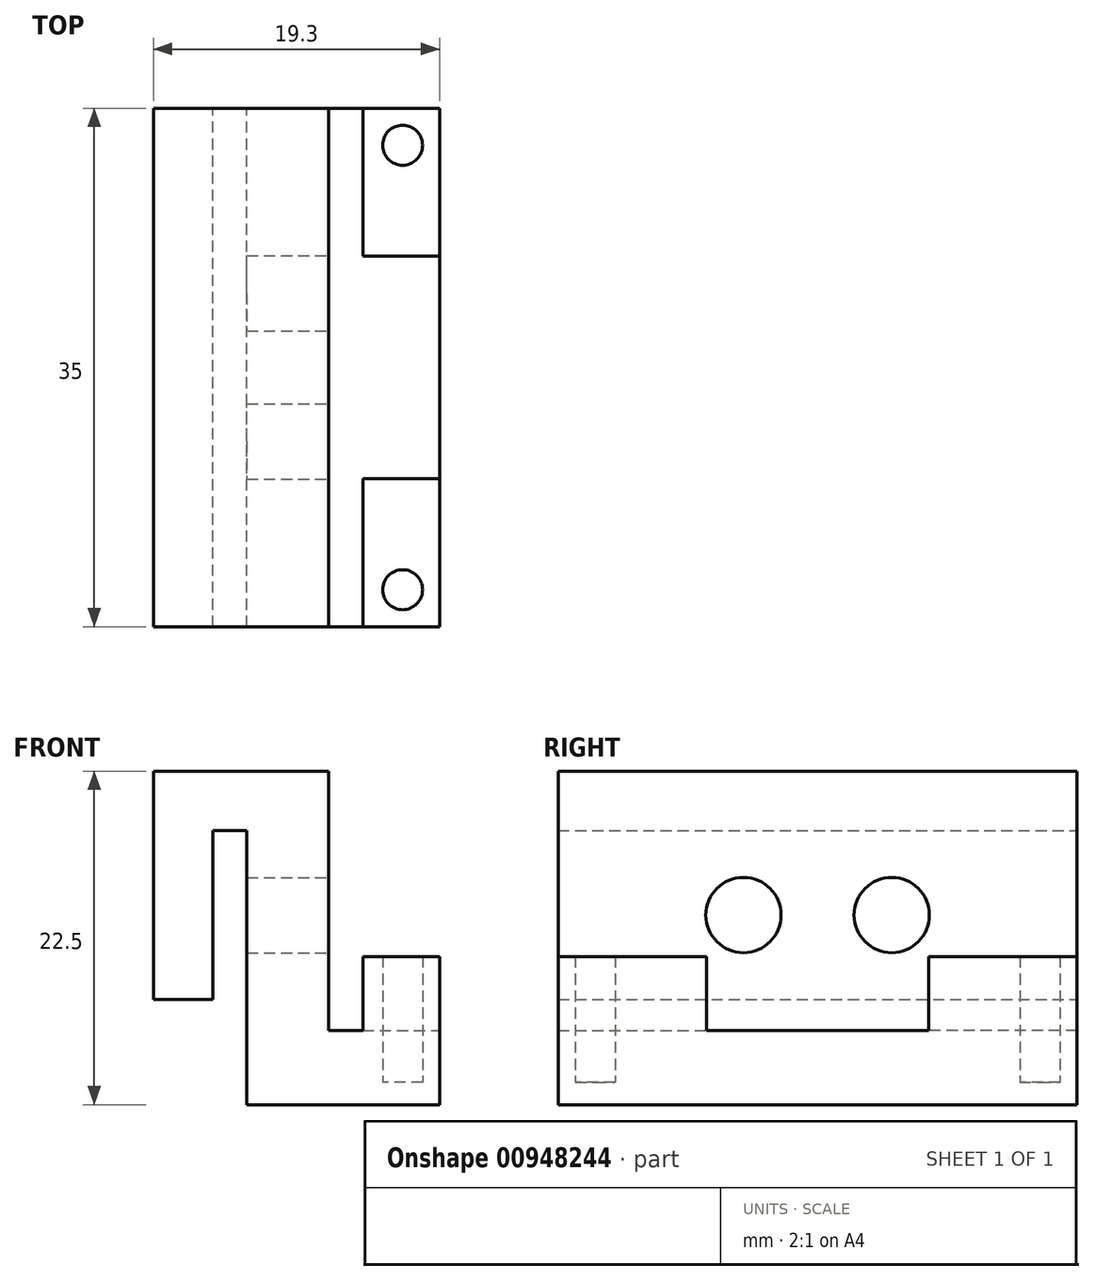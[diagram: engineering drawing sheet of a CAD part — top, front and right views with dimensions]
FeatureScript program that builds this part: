
annotation { "Feature Type Name" : "Feature", "Feature Type Description" : "" }
export const myFeature = defineFeature(function(context is Context, id is Id, definition is map)
    precondition{}
    {
        {
            var Q0;
            Q0=qCreatedBy(makeId("Front.planeOp"),FACE);
            var sketch = newSketch(context, id + "F0", { "sketchPlane" : qUnion([Q0])});
            skLineSegment(sketch, "E0", {"start": v(-36.46, 19.1) * mm, "end": v(-36.46, 34.5) * mm});
            skLineSegment(sketch, "E1", {"start": v(-36.46, 34.5) * mm, "end": v(-24.66, 34.5) * mm});
            skLineSegment(sketch, "E2", {"start": v(-24.66, 34.5) * mm, "end": v(-24.66, 17) * mm});
            skLineSegment(sketch, "E3", {"start": v(-17.16, 12) * mm, "end": v(-30.16, 12) * mm});
            skLineSegment(sketch, "E4", {"start": v(-30.16, 12) * mm, "end": v(-30.16, 30.5) * mm});
            skLineSegment(sketch, "E5", {"start": v(-30.16, 30.5) * mm, "end": v(-32.46, 30.5) * mm});
            skLineSegment(sketch, "E6", {"start": v(-32.46, 30.5) * mm, "end": v(-32.46, 19.1) * mm});
            skLineSegment(sketch, "E7", {"start": v(-32.46, 19.1) * mm, "end": v(-36.46, 19.1) * mm});
            skLineSegment(sketch, "E8", {"start": v(-24.66, 17) * mm, "end": v(-17.16, 17) * mm});
            skLineSegment(sketch, "E9", {"start": v(-17.16, 17) * mm, "end": v(-17.16, 12) * mm});
            skSolve(sketch);
        }
        {
            var Q0;
            Q0=qSketchRegion(id+"F0",true);
            extrude(context, id + "F1", {"entities" : qUnion([Q0]), "depth" : 35 * mm, "offsetDistance" : 25 * mm});
        }
        {
            var Q0;
            Q0=makeQuery(id+"F1.opExtrude","SWEPT_FACE",FACE,{"disambiguationData":[OSD([sQuery(id+"F0.wireOp",EDGE,"E8")])]});
            var sketch = newSketch(context, id + "F2", { "sketchPlane" : qUnion([Q0])});
            skLineSegment(sketch, "E10", {"start": v(-19.66, 0) * mm, "end": v(-19.66, -35) * mm, "construction": true});
            skLineSegment(sketch, "E11", {"start": v(-19.66, -2.5) * mm, "end": v(-17.16, -2.5) * mm, "construction": true});
            skLineSegment(sketch, "E12", {"start": v(-19.66, -32.5) * mm, "end": v(-17.16, -32.5) * mm, "construction": true});
            skLineSegment(sketch, "E13.bottom", {"start": v(-22.34, 0) * mm, "end": v(-17.16, 0) * mm});
            skLineSegment(sketch, "E13.top", {"start": v(-22.34, -10) * mm, "end": v(-17.16, -10) * mm});
            skLineSegment(sketch, "E13.left", {"start": v(-22.34, 0) * mm, "end": v(-22.34, -10) * mm});
            skLineSegment(sketch, "E13.right", {"start": v(-17.16, 0) * mm, "end": v(-17.16, -10) * mm});
            skLineSegment(sketch, "E14.bottom", {"start": v(-22.34, -35) * mm, "end": v(-17.16, -35) * mm});
            skLineSegment(sketch, "E14.top", {"start": v(-22.34, -25) * mm, "end": v(-17.16, -25) * mm});
            skLineSegment(sketch, "E14.left", {"start": v(-22.34, -35) * mm, "end": v(-22.34, -25) * mm});
            skLineSegment(sketch, "E14.right", {"start": v(-17.16, -35) * mm, "end": v(-17.16, -25) * mm});
            skCircle(sketch, "E15", {"center": v(-19.66, -32.5) * mm, "radius": 1.35 * mm});
            skCircle(sketch, "E16", {"center": v(-19.66, -2.5) * mm, "radius": 1.35 * mm});
            skSolve(sketch);
        }
        {
            var Q0;
            Q0=qSketchRegion(id+"F2",true);
            extrude(context, id + "F3", {"entities" : qUnion([Q0]), "operationType" : NewBodyOperationType.ADD, "depth" : 5 * mm, "offsetDistance" : 25 * mm});
        }
        {
            var Q0;
            Q0=makeQuery(id+"F1.opExtrude","SWEPT_FACE",FACE,{"disambiguationData":[OSD([sQuery(id+"F0.wireOp",EDGE,"E2")])]});
            var sketch = newSketch(context, id + "F4", { "sketchPlane" : qUnion([Q0])});
            skLineSegment(sketch, "E17", {"start": v(-35, 24.8) * mm, "end": v(0, 24.8) * mm, "construction": true});
            skLineSegment(sketch, "E18", {"start": v(-22.5, 24.8) * mm, "end": v(-22.5, 34.5) * mm, "construction": true});
            skLineSegment(sketch, "E19", {"start": v(-12.5, 24.8) * mm, "end": v(-12.5, 34.5) * mm, "construction": true});
            skCircle(sketch, "E20", {"center": v(-22.5, 24.8) * mm, "radius": 2.54 * mm});
            skCircle(sketch, "E21", {"center": v(-22.5, 24.8) * mm, "radius": 3.83 * mm});
            skCircle(sketch, "E22", {"center": v(-12.5, 24.8) * mm, "radius": 2.54 * mm});
            skCircle(sketch, "E23", {"center": v(-12.5, 24.8) * mm, "radius": 3.83 * mm});
            skSolve(sketch);
        }
        {
            var Q0;
            Q0=makeQuery(id+"F4.imprint","IMPRINT",FACE,{"disambiguationData":[TD([[makeQuery(id+"F4.imprint","IMPRINT",EDGE,{"derivedFrom":sQuery(id+"F4.wireOp",EDGE,"E20")}),1.0]])]});
            var Q1;
            Q1=makeQuery(id+"F4.imprint","IMPRINT",FACE,{"disambiguationData":[TD([[makeQuery(id+"F4.imprint","IMPRINT",EDGE,{"derivedFrom":sQuery(id+"F4.wireOp",EDGE,"E22")}),1.0]])]});
            extrude(context, id + "F5", {"entities" : qUnion([Q0, Q1]), "operationType" : NewBodyOperationType.REMOVE, "endBound" : BoundingType.UP_TO_NEXT, "oppositeDirection" : true, "depth" : 5.7 * mm, "offsetDistance" : 25 * mm});
        }
        {
            var Q0;
            Q0=makeQuery(id+"F3.boolean.opBoolean","SPLIT",FACE,{"disambiguationData":[TD([makeQuery(id+"F3.opExtrude","SWEPT_FACE",FACE,{"disambiguationData":[OSD([sQuery(id+"F2.wireOp",EDGE,"E15")])]})])],"derivedFrom":makeQuery(id+"F1.opExtrude","SWEPT_FACE",FACE,{"disambiguationData":[OSD([sQuery(id+"F0.wireOp",EDGE,"E8")])]})});
            var Q1;
            Q1=makeQuery(id+"F3.boolean.opBoolean","SPLIT",FACE,{"disambiguationData":[TD([makeQuery(id+"F3.opExtrude","SWEPT_FACE",FACE,{"disambiguationData":[OSD([sQuery(id+"F2.wireOp",EDGE,"E16")])]})])],"derivedFrom":makeQuery(id+"F1.opExtrude","SWEPT_FACE",FACE,{"disambiguationData":[OSD([sQuery(id+"F0.wireOp",EDGE,"E8")])]})});
            extrude(context, id + "F6", {"entities" : qUnion([Q0, Q1]), "operationType" : NewBodyOperationType.REMOVE, "oppositeDirection" : true, "depth" : 3.5 * mm, "offsetDistance" : 25 * mm});
        }
    });
